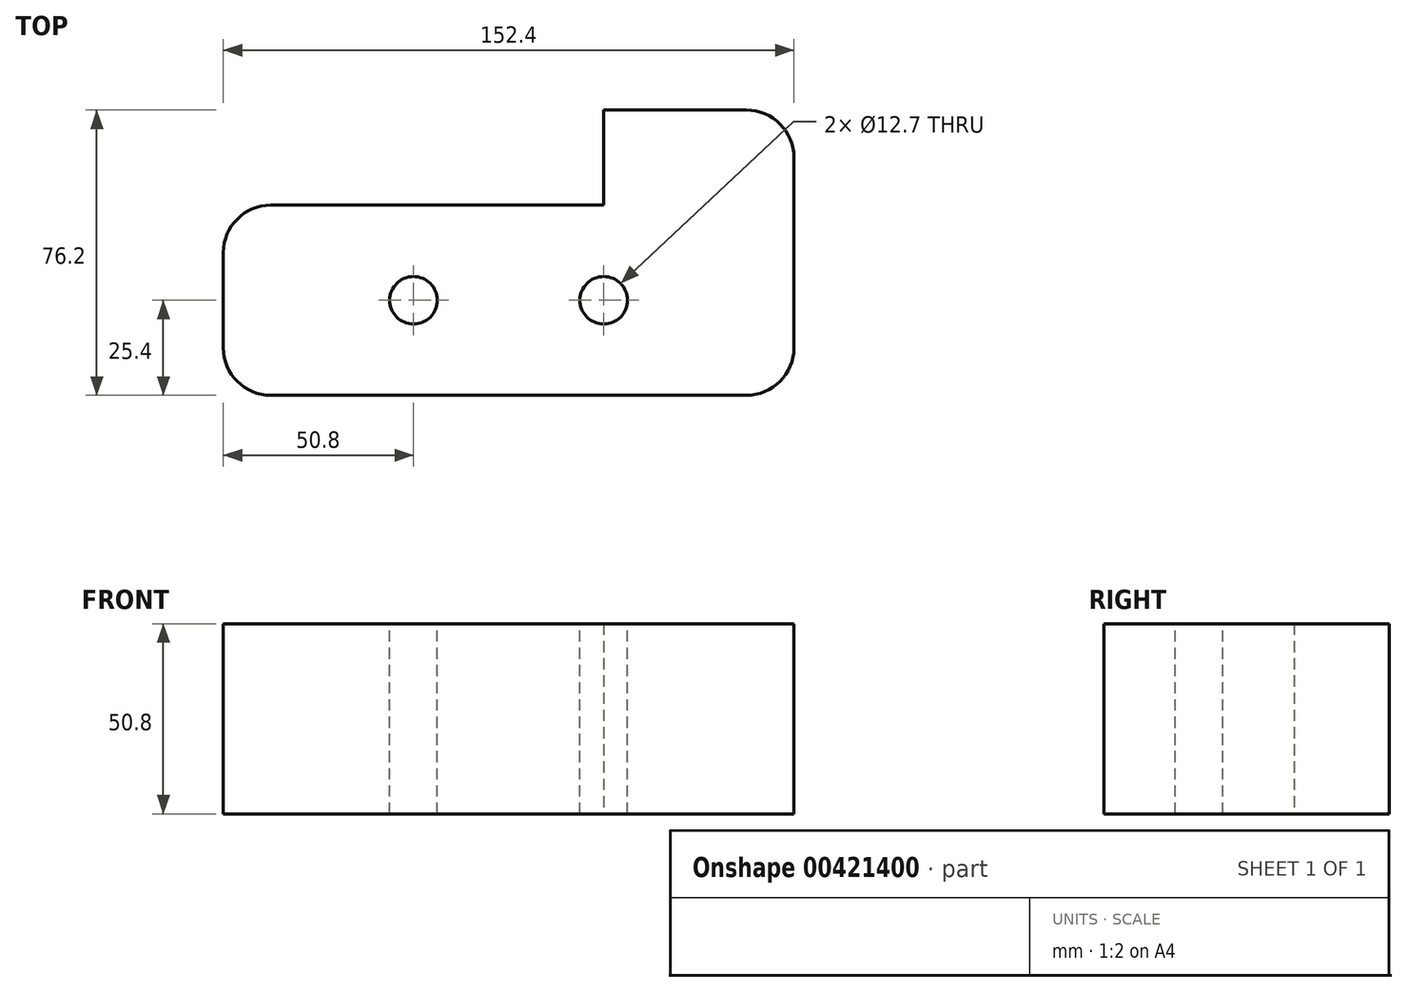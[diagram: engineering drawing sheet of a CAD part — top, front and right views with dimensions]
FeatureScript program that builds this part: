
annotation { "Feature Type Name" : "Feature", "Feature Type Description" : "" }
export const myFeature = defineFeature(function(context is Context, id is Id, definition is map)
    precondition{}
    {
        {
            var Q0;
            Q0=qCreatedBy(makeId("Top.planeOp"),FACE);
            var sketch = newSketch(context, id + "F0", { "sketchPlane" : qUnion([Q0])});
            skLineSegment(sketch, "E0", {"start": v(0, 0) * mm, "end": v(152.4, 0) * mm});
            skLineSegment(sketch, "E1", {"start": v(0, 0) * mm, "end": v(0, 50.8) * mm});
            skLineSegment(sketch, "E2", {"start": v(0, 50.8) * mm, "end": v(101.6, 50.8) * mm});
            skLineSegment(sketch, "E3", {"start": v(101.6, 50.8) * mm, "end": v(101.6, 76.2) * mm});
            skLineSegment(sketch, "E4", {"start": v(101.6, 76.2) * mm, "end": v(152.4, 76.2) * mm});
            skLineSegment(sketch, "E5", {"start": v(152.4, 76.2) * mm, "end": v(152.4, 0) * mm});
            skSolve(sketch);
        }
        {
            var Q0;
            Q0=makeQuery(id+"F0.imprint","IMPRINT",FACE,{"disambiguationData":[TD([[makeQuery(id+"F0.imprint","IMPRINT",EDGE,{"derivedFrom":sQuery(id+"F0.wireOp",EDGE,"E0")}),1.0]])]});
            extrude(context, id + "F1", {"entities" : qUnion([Q0]), "depth" : 50.8 * mm});
        }
        {
            var Q0;
            Q0=makeQuery(id+"F1.opExtrude","SWEPT_EDGE",EDGE,{"disambiguationData":[OSD([sQuery(id+"F0.wireOp",EDGE,"E1"),sQuery(id+"F0.wireOp",EDGE,"E2")])]});
            var Q1;
            Q1=makeQuery(id+"F1.opExtrude","SWEPT_EDGE",EDGE,{"disambiguationData":[OSD([sQuery(id+"F0.wireOp",EDGE,"E4"),sQuery(id+"F0.wireOp",EDGE,"E5")])]});
            var Q2;
            Q2=makeQuery(id+"F1.opExtrude","SWEPT_EDGE",EDGE,{"disambiguationData":[OSD([sQuery(id+"F0.wireOp",EDGE,"E0"),sQuery(id+"F0.wireOp",EDGE,"E5")])]});
            var Q3;
            Q3=makeQuery(id+"F1.opExtrude","SWEPT_EDGE",EDGE,{"disambiguationData":[OSD([sQuery(id+"F0.wireOp",EDGE,"E0"),sQuery(id+"F0.wireOp",EDGE,"E1")])]});
            fillet(context, id + "F2", {"entities" : qUnion([Q0, Q1, Q2, Q3]), "radius" : 12.7 * mm, "tangentPropagation" : true, "allowEdgeOverflow" : false});
        }
        {
            var Q0;
            Q0=makeQuery(id+"F1.opExtrude","CAP_FACE",FACE,{"disambiguationData":[OSD([sQuery(id+"F0.wireOp",EDGE,"E0"),sQuery(id+"F0.wireOp",EDGE,"E1"),sQuery(id+"F0.wireOp",EDGE,"E2"),sQuery(id+"F0.wireOp",EDGE,"E3"),sQuery(id+"F0.wireOp",EDGE,"E4"),sQuery(id+"F0.wireOp",EDGE,"E5")])],"isStart":false});
            var sketch = newSketch(context, id + "F3", { "sketchPlane" : qUnion([Q0])});
            skPoint(sketch, "E6", {"position": v(0, 25.4) * mm});
            skPoint(sketch, "E7", {"position": v(50.8, 25.4) * mm});
            skPoint(sketch, "E8", {"position": v(101.6, 25.4) * mm});
            skSolve(sketch);
        }
        {
            var Q0;
            Q0=sQuery(id+"F3.wireOp",VERTEX,"E7");
            var Q1;
            Q1=sQuery(id+"F3.wireOp",VERTEX,"E8");
            var Q2;
            Q2=makeQuery(id+"F1.opExtrude","SWEPT_BODY",BODY,{"disambiguationData":[OSD([sQuery(id+"F0.wireOp",EDGE,"E0"),sQuery(id+"F0.wireOp",EDGE,"E1"),sQuery(id+"F0.wireOp",EDGE,"E2"),sQuery(id+"F0.wireOp",EDGE,"E3"),sQuery(id+"F0.wireOp",EDGE,"E4"),sQuery(id+"F0.wireOp",EDGE,"E5")])]});
            hole(context, id + "F4", {"style" : HoleStyle.SIMPLE, "endStyle" : HoleEndStyle.THROUGH, "holeDiameter" : 12.7 * mm, "isTappedThrough" : true, "tappedDepth" : 12.7 * mm, "tapClearance" : 3, "locations" : qUnion([Q0, Q1]), "scope" : qUnion([Q2])});
        }
    });
